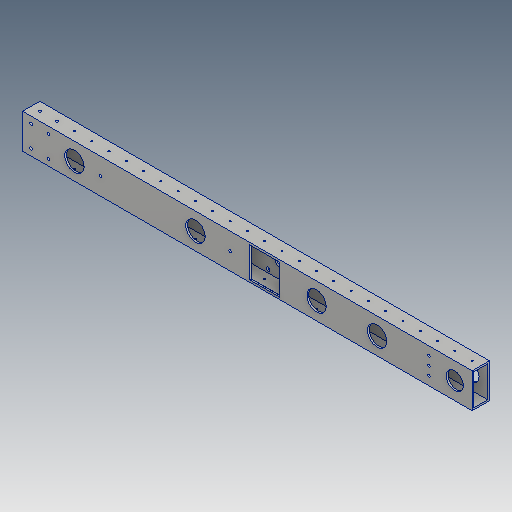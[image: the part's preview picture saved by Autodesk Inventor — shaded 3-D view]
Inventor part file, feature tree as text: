
AUTODESK INVENTOR PART (.ipt)
format: ipt  version: 2018 (Build 220112000, 112)  size: 291,840 bytes
history: native  units: in
note: dims shown in document units (in); Inventor stores cm internally (conversion verified against a paired STEP export)
features: sketch x16, hole x9, reference x8, extrude x7, other x6, shell x1, projected_geometry x1
ambient origin geometry x8: Origin, YZ Plane, XZ Plane, XY Plane, X Axis, Y Axis, Z Axis, Center Point
bodies: Solid1 (feature_tree)
feature tree (48):
  extrude  "Extrusion1"  Depth=2.0in
  shell  "Shell1"  Thickness=24.0in
  hole  "Hole1"  [1 undecoded]
  hole  "Hole5"  [1 undecoded]
  hole  "Hole6"  [1 undecoded]
  extrude  "Extrusion2"  Depth=1.0in
  hole  "Hole7"  [1 undecoded]
  extrude  "Extrusion3"  Depth=0.5in TaperAngle=0.0deg
  hole  "Hole8"  [1 undecoded]
  hole  "Hole9"  [1 undecoded]
  hole  "Hole10"  [1 undecoded]
  extrude  "Extrusion4"  Depth=0.5in
  hole  "Hole11"  [1 undecoded]
  hole  "Hole12"  [1 undecoded]
  extrude  "Extrusion5"  Depth=2.0in
  extrude  "Extrusion6"  Depth=2.0in
  extrude  "Extrusion7"  Depth=1.0in
  sketch  "Sketch1"  dims[d0=1.0in d1=2.0in d2=24.0in d3=0.0in]
  sketch  "Sketch2"  dims[d4=0.1in d5=0.5in]
  sketch  "Sketch6"  dims[d6=0.5in d7=14.5669in d9=1.0in d10=0.3937in d12=1.0in]
  sketch  "Sketch7"  dims[d14=0.1in d15=0.75in d16=0.375in d17=0.25in d18=0.5635in d19=2.0in d20=0.8108in d48=12.0in]
  sketch  "Sketch8"  dims[d49=1.0in]
  sketch  "Sketch9"  dims[d50=0.625in d51=0.75in d52=0.375in d53=0.25in d54=0.5635in d55=1.0in d56=0.8108in d57=1.0in]
  reference  "Reference3"
  reference  "Reference4"
  reference  "Reference5"
  reference  "Reference6"
  sketch  "Sketch10"  dims[d58=11.0in]
  projected_geometry  "Projected Loop2"
  sketch  "Sketch11"  dims[d59=1.0in d60=0.75in d61=0.375in d62=0.25in d63=0.5635in d64=1.0in d65=0.8108in d66=1.75in]
  sketch  "Sketch12"  dims[d67=1.75in d68=0.5in d69=0.0in]
  reference  "Reference7"
  sketch  "Sketch13"  dims[d70=0.221in d71=0.75in d72=0.385in d73=0.25in d74=0.5635in d75=1.0in d76=0.8108in d77=2.0in d78=0.0in]
  reference  "Reference8"
  sketch  "Sketch14"  dims[d79=1.0in d80=1.0in]
  reference  "Reference9"
  sketch  "Sketch15"  dims[d81=0.5in d82=0.5in]
  sketch  "Sketch16"  dims[d83=0.154in d84=0.75in d85=0.252in d86=0.25in d87=0.5635in d88=2.0in d89=0.8108in d90=0.5in]
  reference  "Reference10"
  sketch  "Sketch17"  dims[d91=0.5in]
  sketch  "Sketch18"  dims[d92=0.154in d93=0.75in d94=0.252in d95=0.25in d96=0.5635in d97=2.0in d98=0.8108in]
  sketch  "Sketch19"  dims[d99=0.154in d100=0.75in d101=0.252in d102=0.25in d103=0.5635in d104=2.0in d105=0.8108in d106=0.0in d107=0.0in d108=2.5in d109=1.125in d110=1.0in d111=2.0in d112=0.0in d113=1.0in d114=12.0in d115=0.154in d116=0.75in d117=0.252in d118=0.25in d119=0.5635in d120=2.0in d121=0.8108in d122=0.154in d123=0.75in d124=0.252in d125=0.25in d126=0.5635in d127=2.0in d128=0.8108in d129=1.125in d130=1.0in d131=3.0in d132=2.0in d133=0.0in d134=1.125in d135=1.0in d136=14.0in d137=2.0in d138=0.0in d139=1.0in d140=7.0in d141=1.125in d142=2.0in d143=0.0in]
  parser-record x1  (decoder bookkeeping rows leaked as tree rows — omitted from the tree; the rows remain in map.json)
  other  "Robot.iam"
  other  "VersaPlanetary_v2_Two_Stage_100_1_with_BAG:1"
  other  "cross bar 2:2"
  other  "Drive Frame Rail:2"
  other  "cross bar 2:4"
note: 9 required parameter values undecoded (feature->parameter linkage not recoverable at this tier; creation-order binding heuristic only, values carry confidence <= 0.55)
note: 1 file-system path scrubbed to <path> (originals preserved in map.json)
